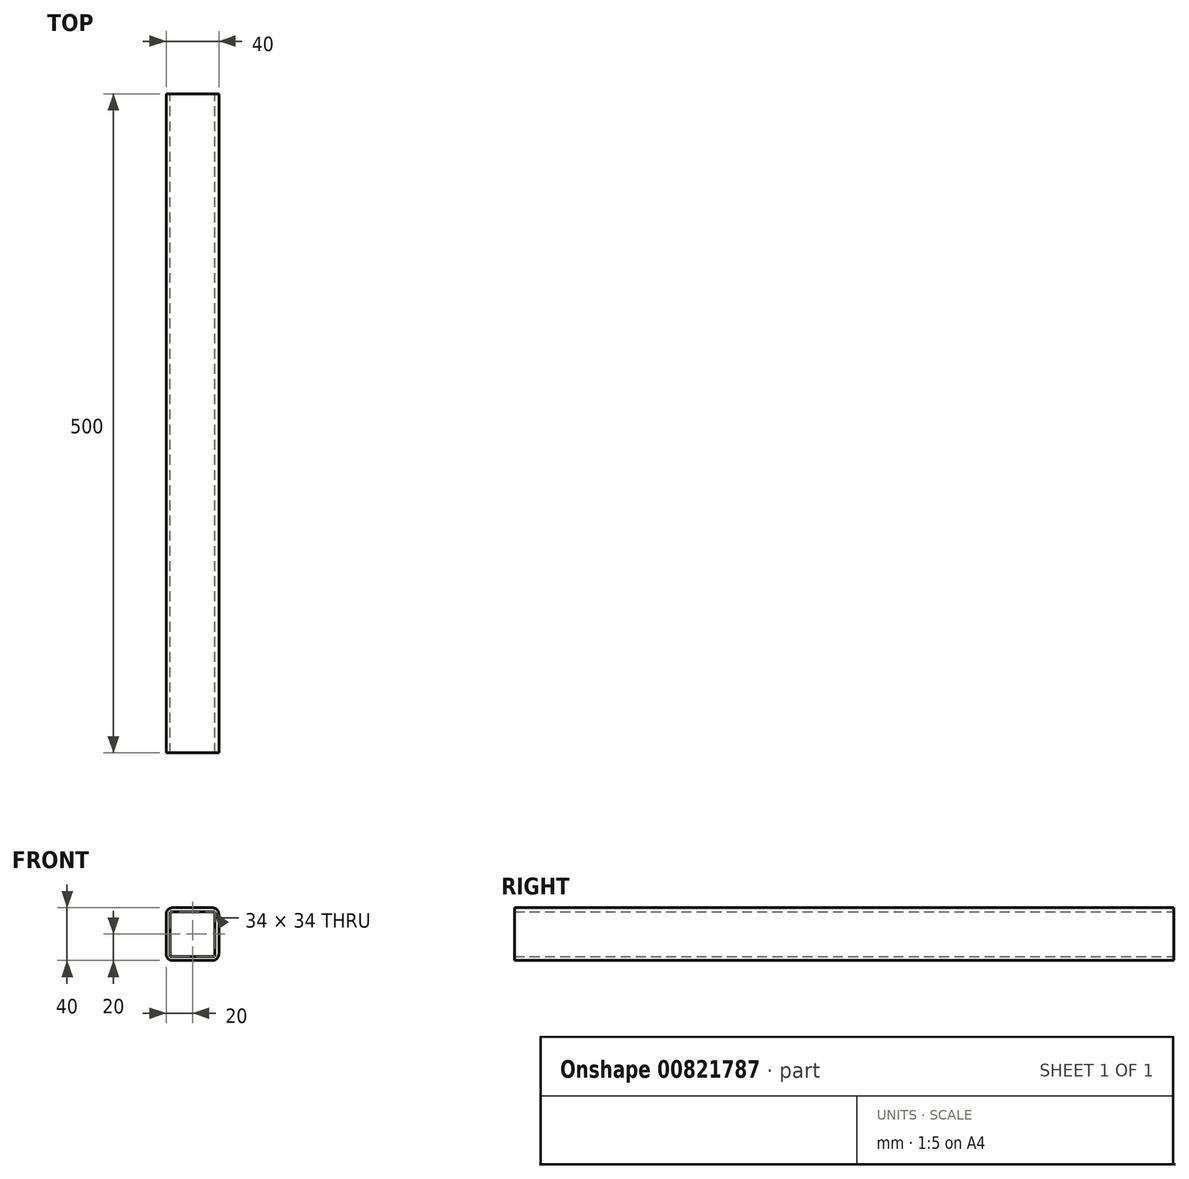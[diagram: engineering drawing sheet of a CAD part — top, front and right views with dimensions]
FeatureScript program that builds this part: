
annotation { "Feature Type Name" : "Feature", "Feature Type Description" : "" }
export const myFeature = defineFeature(function(context is Context, id is Id, definition is map)
    precondition{}
    {
        {
            assignVariable(context, id + "F0", {"name" : "x_bar_length", "anyValue" : 500 * mm});
        }
        {
            var Q0;
            Q0=qCreatedBy(makeId("Front.planeOp"),FACE);
            var sketch = newSketch(context, id + "F1", { "sketchPlane" : qUnion([Q0])});
            skLineSegment(sketch, "E0.bottom", {"start": v(15, 20) * mm, "end": v(-15, 20) * mm});
            skLineSegment(sketch, "E0.top", {"start": v(15, -20) * mm, "end": v(-15, -20) * mm});
            skLineSegment(sketch, "E0.left", {"start": v(20, 15) * mm, "end": v(20, -15) * mm});
            skLineSegment(sketch, "E0.right", {"start": v(-20, 15) * mm, "end": v(-20, -15) * mm});
            skPoint(sketch, "E0.middle", {"position": v(0, 0) * mm});
            skPoint(sketch, "E1.visualSharp", {"position": v(-20, 20) * mm});
            skArc(sketch, "E1.filletArc", {"start": v(-15, 20) * mm, "mid": v(-18.54, 18.54) * mm, "end": v(-20, 15) * mm});
            skPoint(sketch, "E2.visualSharp", {"position": v(20, 20) * mm});
            skArc(sketch, "E2.filletArc", {"start": v(20, 15) * mm, "mid": v(18.54, 18.54) * mm, "end": v(15, 20) * mm});
            skPoint(sketch, "E3.visualSharp", {"position": v(20, -20) * mm});
            skArc(sketch, "E3.filletArc", {"start": v(15, -20) * mm, "mid": v(18.54, -18.54) * mm, "end": v(20, -15) * mm});
            skPoint(sketch, "E4.visualSharp", {"position": v(-20, -20) * mm});
            skArc(sketch, "E4.filletArc", {"start": v(-20, -15) * mm, "mid": v(-18.54, -18.54) * mm, "end": v(-15, -20) * mm});
            skLineSegment(sketch, "E5.0", {"start": v(-17, 17) * mm, "end": v(-17, -17) * mm});
            skLineSegment(sketch, "E5.1", {"start": v(17, 17) * mm, "end": v(-17, 17) * mm});
            skLineSegment(sketch, "E5.2", {"start": v(17, 17) * mm, "end": v(17, -17) * mm});
            skLineSegment(sketch, "E5.3", {"start": v(17, -17) * mm, "end": v(-17, -17) * mm});
            skSolve(sketch);
        }
        {
            var Q0;
            Q0=qSketchRegion(id+"F1",true);
            extrude(context, id + "F2", {"entities" : qUnion([Q0]), "depth" : getVariable(context, 'x_bar_length'), "offsetDistance" : 25 * mm});
        }
    });
